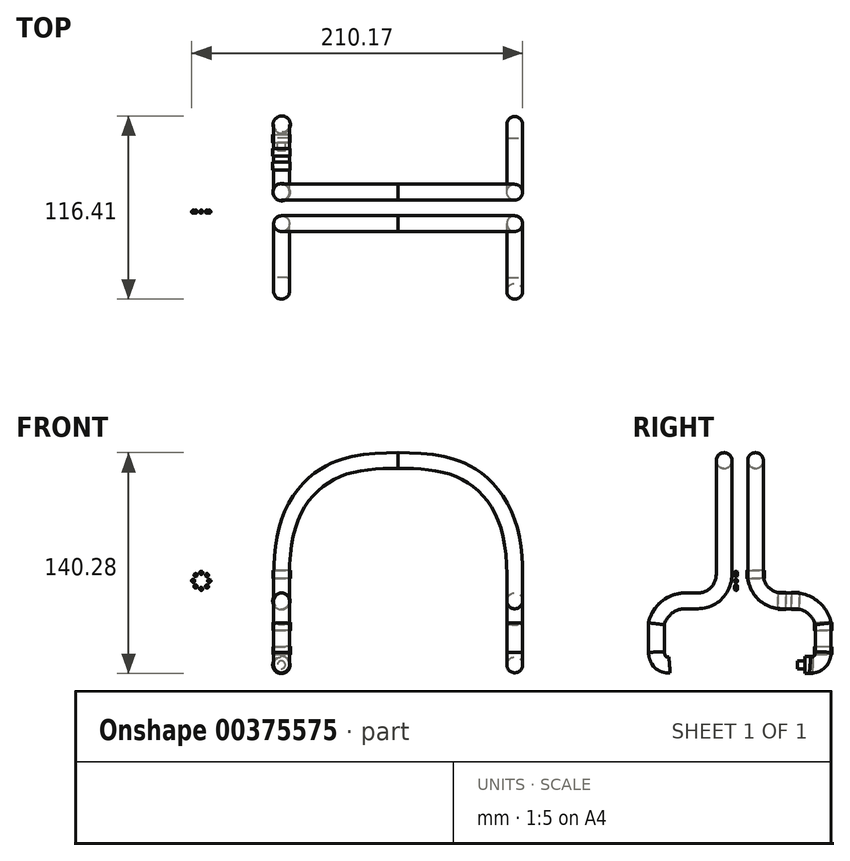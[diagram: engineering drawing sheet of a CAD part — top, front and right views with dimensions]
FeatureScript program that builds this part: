
annotation { "Feature Type Name" : "Feature", "Feature Type Description" : "" }
export const myFeature = defineFeature(function(context is Context, id is Id, definition is map)
    precondition{}
    {
        {
            var Q0;
            Q0=qCreatedBy(makeId("Front.planeOp"),FACE);
            var sketch = newSketch(context, id + "F0", { "sketchPlane" : qUnion([Q0])});
            skFitSpline(sketch, "E0", {"points": [v(0, 72.42) * mm, v(-33.4, 68.8) * mm, v(-57.94, 53.1) * mm, v(-74.03, 0) * mm], "startDerivative": vector(-111.78, 0.22) * mm, "endDerivative": vector(0, -202.38) * mm});
            skLineSegment(sketch, "E1", {"start": v(-74.03, 0) * mm, "end": v(-74.03, 60.8) * mm, "construction": true});
            skSolve(sketch);
        }
        {
            var Q0;
            Q0=sQuery(id+"F0.wireOp",EDGE,"E1");
            cPlane(context, id + "F1", {"entities" : qUnion([Q0]), "cplaneType" : CPlaneType.LINE_ANGLE, "offset" : 25 * mm, "angle" : 0 * degree, "width" : 150 * mm, "height" : 150 * mm});
        }
        {
            var Q0;
            Q0=qCreatedBy(id+"F1.planeOp",FACE);
            var sketch = newSketch(context, id + "F2", { "sketchPlane" : qUnion([Q0])});
            skLineSegment(sketch, "E2", {"start": v(16.67, -16.67) * mm, "end": v(24.63, -16.67) * mm});
            skArc(sketch, "E3", {"start": v(43, -31.22) * mm, "mid": v(36.35, -20.75) * mm, "end": v(24.63, -16.67) * mm});
            skArc(sketch, "E4", {"start": v(0, 0) * mm, "mid": v(4.88, -11.79) * mm, "end": v(16.67, -16.67) * mm});
            skLineSegment(sketch, "E5", {"start": v(43, -31.22) * mm, "end": v(43, -49.22) * mm});
            skFitSpline(sketch, "E6", {"points": [v(43, -49.22) * mm, v(34.64, -57.34) * mm], "startDerivative": vector(-0.5, -11.79) * mm, "endDerivative": vector(-18.5, 1.47) * mm});
            skSolve(sketch);
        }
        {
            var Q0;
            Q0=qCreatedBy(makeId("Right.planeOp"),FACE);
            var sketch = newSketch(context, id + "F3", { "sketchPlane" : qUnion([Q0])});
            skCircle(sketch, "E7", {"center": v(0, 72.42) * mm, "radius": 5 * mm});
            skSolve(sketch);
        }
        {
            var Q0;
            Q0=makeQuery(id+"F3.imprint","IMPRINT",FACE,{"disambiguationData":[TD([[makeQuery(id+"F3.imprint","IMPRINT",EDGE,{"derivedFrom":sQuery(id+"F3.wireOp",EDGE,"E7")}),1.0]])]});
            var Q1;
            Q1=sQuery(id+"F0.wireOp",EDGE,"E0");
            var Q2;
            Q2=sQuery(id+"F2.wireOp",EDGE,"E4");
            var Q3;
            Q3=sQuery(id+"F2.wireOp",EDGE,"E2");
            var Q4;
            Q4=sQuery(id+"F2.wireOp",EDGE,"E3");
            var Q5;
            Q5=sQuery(id+"F2.wireOp",EDGE,"kxrQsheS-czUh-oxnq-51k7-gvsOdt4erGw2");
            var Q6;
            Q6=sQuery(id+"F2.wireOp",EDGE,"E5");
            var Q7;
            Q7=sQuery(id+"F2.wireOp",EDGE,"14SF9fJG-ZFTD-wqYl-jZCY-3tKnJQsrrfNn");
            var Q8;
            Q8=sQuery(id+"F2.wireOp",EDGE,"d9A6EsEj-tuIw-lgPH-8lYu-oR9HDDNZeIlY");
            var Q9;
            Q9=sQuery(id+"F2.wireOp",EDGE,"E6");
            sweep(context, id + "F4", {"profiles" : qUnion([Q0]), "path" : qUnion([Q1, Q2, Q3, Q4, Q5, Q6, Q7, Q8, Q9])});
        }
        {
            var Q0;
            Q0=qCreatedBy(makeId("Front.planeOp"),FACE);
            var sketch = newSketch(context, id + "F5", { "sketchPlane" : qUnion([Q0])});
            skCircle(sketch, "E8", {"center": v(-125.04, -3.96) * mm, "radius": 5.5 * mm});
            skSolve(sketch);
        }
        {
            var Q0;
            Q0=makeQuery(id+"F5.imprint","IMPRINT",FACE,{"disambiguationData":[TD([[makeQuery(id+"F5.imprint","IMPRINT",EDGE,{"derivedFrom":sQuery(id+"F5.wireOp",EDGE,"E8")}),1.0]])]});
            extrude(context, id + "F6", {"entities" : qUnion([Q0]), "depth" : 5 * mm});
        }
        {
            var Q0;
            Q0=qCreatedBy(makeId("Front.planeOp"),FACE);
            var sketch = newSketch(context, id + "F7", { "sketchPlane" : qUnion([Q0])});
            skLineSegment(sketch, "E9", {"start": v(-174.04, -0.03) * mm, "end": v(-174.04, -2.03) * mm});
            skArc(sketch, "E10", {"start": v(-174.04, -0.03) * mm, "mid": v(-175.04, -1.03) * mm, "end": v(-174.04, -2.03) * mm});
            skPoint(sketch, "E11.orphan", {"position": v(-174.04, 7.2) * mm});
            skPoint(sketch, "E12.orphan", {"position": v(-174.04, -9.26) * mm});
            skSolve(sketch);
        }
        {
            var Q0;
            Q0 = qSketchRegion(id + "F7", true);
            var Q1;
            Q1=sQuery(id+"F7.wireOp",EDGE,"E9");
            revolve(context, id + "F8", {"entities" : qUnion([Q0]), "axis" : qUnion([Q1]), "revolveType" : RevolveType.FULL});
        }
        {
            var Q0;
            Q0=makeQuery(id+"F8.opRevolve","SWEPT_BODY",BODY,{"disambiguationData":[OSD([sQuery(id+"F7.wireOp",EDGE,"E9"),sQuery(id+"F7.wireOp",EDGE,"E10")])]});
            transform(context, id + "F9", {"entities" : qUnion([Q0]), "transformType" : TransformType.TRANSLATION_3D, "dx" : 43.9 * mm, "dy" : -2.4 * mm, "dz" : -2.9 * mm, "makeCopy" : false});
        }
        {
            var Q0;
            Q0=makeQuery(id+"F8.opRevolve","SWEPT_BODY",BODY,{"disambiguationData":[OSD([sQuery(id+"F7.wireOp",EDGE,"E9"),sQuery(id+"F7.wireOp",EDGE,"E10")])]});
            var Q1;
            Q1=makeQuery(id+"F6.opExtrude","CAP_EDGE",EDGE,{"disambiguationData":[OSD([sQuery(id+"F5.wireOp",EDGE,"E8")])],"isStart":false});
            circularPattern(context, id + "F10", {"entities" : qUnion([Q0]), "axis" : qUnion([Q1]), "angle" : 360 * degree, "instanceCount" : 8, "equalSpace" : true});
        }
        {
            var Q0;
            Q0=makeQuery(id+"F4.opSweep","SWEPT_BODY",BODY,{"disambiguationData":[OSD([sQuery(id+"F2.wireOp",EDGE,"14SF9fJG-ZFTD-wqYl-jZCY-3tKnJQsrrfNn"),sQuery(id+"F3.wireOp",EDGE,"E7")])]});
            var Q1;
            Q1=makeQuery(id+"F6.opExtrude","SWEPT_BODY",BODY,{"disambiguationData":[OSD([sQuery(id+"F5.wireOp",EDGE,"E8")])]});
            var Q2;
            Q2=makeQuery(id+"FVSApvK7jGI9yFo_2.opPattern","COPY",BODY,{"derivedFrom":makeQuery(id+"F6.opExtrude","SWEPT_BODY",BODY,{"disambiguationData":[OSD([sQuery(id+"F5.wireOp",EDGE,"E8")])]}),"instanceName":"1"});
            var Q3;
            Q3=makeQuery(id+"FmmTDmjITJztVAW_2.opPattern","COPY",BODY,{"derivedFrom":makeQuery(id+"FVSApvK7jGI9yFo_2.opPattern","COPY",BODY,{"derivedFrom":makeQuery(id+"F6.opExtrude","SWEPT_BODY",BODY,{"disambiguationData":[OSD([sQuery(id+"F5.wireOp",EDGE,"E8")])]}),"instanceName":"1"}),"instanceName":"1"});
            transform(context, id + "F11", {"entities" : qUnion([Q0, Q1, Q2, Q3]), "transformType" : TransformType.TRANSLATION_3D, "dx" : 0 * mm, "dy" : 10 * mm, "dz" : 0 * mm, "makeCopy" : false});
        }
        {
            var Q0;
            Q0=makeQuery(id+"F6.opExtrude","SWEPT_BODY",BODY,{"disambiguationData":[OSD([sQuery(id+"F5.wireOp",EDGE,"E8")])]});
            transform(context, id + "F12", {"entities" : qUnion([Q0]), "transformType" : TransformType.TRANSLATION_3D, "dx" : 50.9 * mm, "dy" : 36.5 * mm, "dz" : -53.4 * mm, "makeCopy" : false});
        }
        {
            var Q0;
            Q0=makeQuery(id+"F6.opExtrude","SWEPT_BODY",BODY,{"disambiguationData":[OSD([sQuery(id+"F5.wireOp",EDGE,"E8")])]});
            var Q1;
            Q1=makeQuery(id+"F4.opSweep","MID_CAP_EDGE",EDGE,{"disambiguationData":[OSD([sQuery(id+"F2.wireOp",VERTEX,"E3.end"),sQuery(id+"F3.wireOp",EDGE,"E7")])],"capPos":3.0});
            transform(context, id + "F13", {"entities" : qUnion([Q0]), "transformType" : TransformType.ROTATION, "transformAxis" : qUnion([Q1]), "angle" : 90 * degree, "makeCopy" : true});
        }
        {
            var Q0;
            Q0=makeQuery(id+"F13.opPattern","COPY",BODY,{"derivedFrom":makeQuery(id+"F6.opExtrude","SWEPT_BODY",BODY,{"disambiguationData":[OSD([sQuery(id+"F5.wireOp",EDGE,"E8")])]}),"instanceName":"1"});
            var Q1;
            Q1=makeQuery(id+"F4.opSweep","MID_CAP_EDGE",EDGE,{"disambiguationData":[OSD([sQuery(id+"F2.wireOp",VERTEX,"E4.start"),sQuery(id+"F3.wireOp",EDGE,"E7")])],"capPos":1.0});
            transform(context, id + "F14", {"entities" : qUnion([Q0]), "transformType" : TransformType.ROTATION, "transformAxis" : qUnion([Q1]), "angle" : 90 * degree, "makeCopy" : false});
        }
        {
            var Q0;
            Q0=makeQuery(id+"F13.opPattern","COPY",BODY,{"derivedFrom":makeQuery(id+"F6.opExtrude","SWEPT_BODY",BODY,{"disambiguationData":[OSD([sQuery(id+"F5.wireOp",EDGE,"E8")])]}),"instanceName":"1"});
            var Q1;
            Q1=makeQuery(id+"F4.opSweep","MID_CAP_EDGE",EDGE,{"disambiguationData":[OSD([sQuery(id+"F2.wireOp",VERTEX,"E3.end"),sQuery(id+"F3.wireOp",EDGE,"E7")])],"capPos":3.0});
            transform(context, id + "F15", {"entities" : qUnion([Q0]), "transformType" : TransformType.ROTATION, "transformAxis" : qUnion([Q1]), "angle" : 90 * degree, "makeCopy" : false});
        }
        {
            var Q0;
            Q0=makeQuery(id+"F13.opPattern","COPY",BODY,{"derivedFrom":makeQuery(id+"F6.opExtrude","SWEPT_BODY",BODY,{"disambiguationData":[OSD([sQuery(id+"F5.wireOp",EDGE,"E8")])]}),"instanceName":"1"});
            transform(context, id + "F16", {"entities" : qUnion([Q0]), "transformType" : TransformType.TRANSLATION_3D, "dx" : -0.2 * mm, "dy" : 2.3 * mm, "dz" : 2.3 * mm, "makeCopy" : false});
        }
        {
            var Q0;
            Q0=makeQuery(id+"F13.opPattern","COPY",BODY,{"derivedFrom":makeQuery(id+"F6.opExtrude","SWEPT_BODY",BODY,{"disambiguationData":[OSD([sQuery(id+"F5.wireOp",EDGE,"E8")])]}),"instanceName":"1"});
            transform(context, id + "F17", {"entities" : qUnion([Q0]), "transformType" : TransformType.TRANSLATION_3D, "dx" : 0 * mm, "dy" : 0 * mm, "dz" : 15.3 * mm, "makeCopy" : true});
        }
        {
            var Q0;
            Q0=makeQuery(id+"F6.opExtrude","SWEPT_BODY",BODY,{"disambiguationData":[OSD([sQuery(id+"F5.wireOp",EDGE,"E8")])]});
            transform(context, id + "F18", {"entities" : qUnion([Q0]), "transformType" : TransformType.TRANSLATION_3D, "dx" : 0 * mm, "dy" : -8.7 * mm, "dz" : 40.6 * mm, "makeCopy" : true});
        }
        {
            var Q0;
            Q0=makeQuery(id+"F18.opPattern","COPY",BODY,{"derivedFrom":makeQuery(id+"F6.opExtrude","SWEPT_BODY",BODY,{"disambiguationData":[OSD([sQuery(id+"F5.wireOp",EDGE,"E8")])]}),"instanceName":"1"});
            transform(context, id + "F19", {"entities" : qUnion([Q0]), "transformType" : TransformType.TRANSLATION_3D, "dx" : 0 * mm, "dy" : -8.6 * mm, "dz" : 0 * mm, "makeCopy" : true});
        }
        {
            var Q0;
            Q0=makeQuery(id+"F13.opPattern","COPY",BODY,{"derivedFrom":makeQuery(id+"F6.opExtrude","SWEPT_BODY",BODY,{"disambiguationData":[OSD([sQuery(id+"F5.wireOp",EDGE,"E8")])]}),"instanceName":"1"});
            transform(context, id + "F20", {"entities" : qUnion([Q0]), "transformType" : TransformType.TRANSLATION_3D, "dx" : 0 * mm, "dy" : -42.9 * mm, "dz" : 48.4 * mm, "makeCopy" : true});
        }
        {
            var Q0;
            Q0=makeQuery(id+"F6.opExtrude","CAP_FACE",FACE,{"disambiguationData":[OSD([sQuery(id+"F5.wireOp",EDGE,"E8")])],"isStart":false});
            var sketch = newSketch(context, id + "F21", { "sketchPlane" : qUnion([Q0])});
            skCircle(sketch, "E13", {"center": v(-74.14, -57.36) * mm, "radius": 2.5 * mm});
            skSolve(sketch);
        }
        {
            var Q0;
            Q0=makeQuery(id+"F21.imprint","IMPRINT",FACE,{"disambiguationData":[TD([[makeQuery(id+"F21.imprint","IMPRINT",EDGE,{"derivedFrom":sQuery(id+"F21.wireOp",EDGE,"E13")}),1.0]])]});
            extrude(context, id + "F22", {"entities" : qUnion([Q0]), "operationType" : NewBodyOperationType.ADD, "depth" : 5 * mm});
        }
        {
            var Q0;
            Q0=makeQuery(id+"F4.opSweep","SWEPT_BODY",BODY,{"disambiguationData":[OSD([sQuery(id+"F2.wireOp",EDGE,"E6"),sQuery(id+"F3.wireOp",EDGE,"E7")])]});
            var Q1;
            Q1=qCreatedBy(makeId("Front.planeOp"),FACE);
            mirror(context, id + "F23", {"entities" : qUnion([Q0]), "mirrorPlane" : qUnion([Q1])});
        }
        {
            var Q0;
            Q0=makeQuery(id+"F4.opSweep","SWEPT_BODY",BODY,{"disambiguationData":[OSD([sQuery(id+"F2.wireOp",EDGE,"E6"),sQuery(id+"F3.wireOp",EDGE,"E7")])]});
            var Q1;
            Q1=makeQuery(id+"F23.opPattern","COPY",BODY,{"derivedFrom":makeQuery(id+"F4.opSweep","SWEPT_BODY",BODY,{"disambiguationData":[OSD([sQuery(id+"F2.wireOp",EDGE,"E6"),sQuery(id+"F3.wireOp",EDGE,"E7")])]}),"instanceName":"1"});
            var Q2;
            Q2=qCreatedBy(makeId("Right.planeOp"),FACE);
            mirror(context, id + "F24", {"entities" : qUnion([Q0, Q1]), "mirrorPlane" : qUnion([Q2])});
        }
    });
